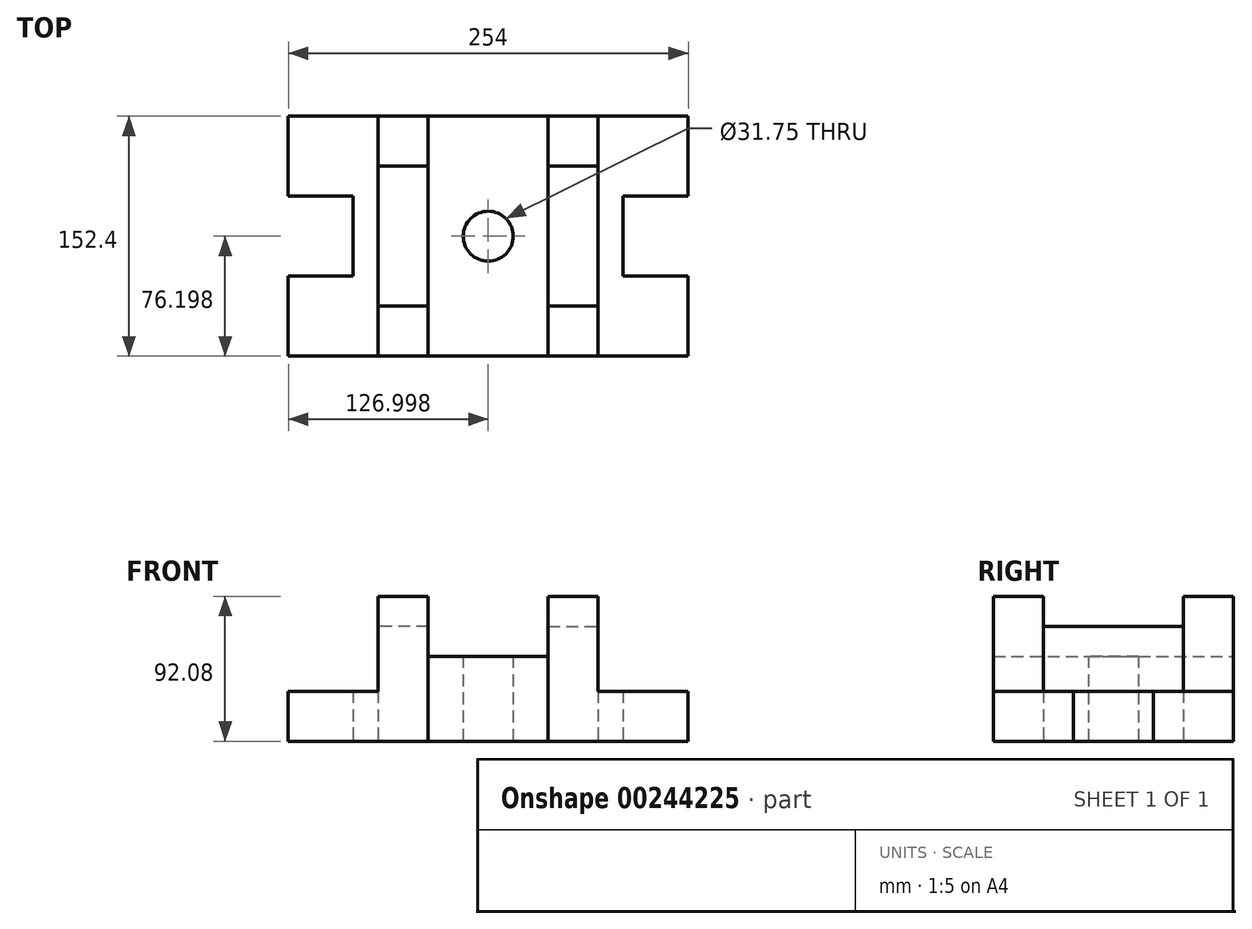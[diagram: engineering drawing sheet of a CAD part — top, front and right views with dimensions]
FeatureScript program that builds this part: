
annotation { "Feature Type Name" : "Feature", "Feature Type Description" : "" }
export const myFeature = defineFeature(function(context is Context, id is Id, definition is map)
    precondition{}
    {
        {
            var Q0;
            Q0=qCreatedBy(makeId("Top.planeOp"),FACE);
            var sketch = newSketch(context, id + "F0", { "sketchPlane" : qUnion([Q0])});
            skLineSegment(sketch, "E0.bottom", {"start": v(-146.62, 99.6) * mm, "end": v(107.38, 99.6) * mm});
            skLineSegment(sketch, "E0.top", {"start": v(-146.62, -52.8) * mm, "end": v(107.38, -52.8) * mm});
            skLineSegment(sketch, "E0.left", {"start": v(-146.62, 99.6) * mm, "end": v(-146.62, -52.8) * mm});
            skLineSegment(sketch, "E0.right", {"start": v(107.38, 99.6) * mm, "end": v(107.38, -52.8) * mm});
            skLineSegment(sketch, "E1", {"start": v(66.1, -2) * mm, "end": v(107.38, -2) * mm});
            skLineSegment(sketch, "E2", {"start": v(66.1, -2) * mm, "end": v(66.1, 48.8) * mm});
            skLineSegment(sketch, "E3", {"start": v(66.1, 48.8) * mm, "end": v(107.38, 48.8) * mm});
            skLineSegment(sketch, "E4", {"start": v(-19.62, -52.8) * mm, "end": v(-19.62, 99.6) * mm, "construction": true});
            skLineSegment(sketch, "E5.MirrorCS", {"start": v(-105.35, -2) * mm, "end": v(-105.35, 48.8) * mm});
            skLineSegment(sketch, "E6.MirrorCS", {"start": v(-105.35, 48.8) * mm, "end": v(-146.62, 48.8) * mm});
            skLineSegment(sketch, "E7.MirrorCS", {"start": v(-105.35, -2) * mm, "end": v(-146.62, -2) * mm});
            skLineSegment(sketch, "E8", {"start": v(50.23, -52.8) * mm, "end": v(50.23, 99.6) * mm});
            skLineSegment(sketch, "E9", {"start": v(18.48, -52.8) * mm, "end": v(18.48, 99.6) * mm});
            skLineSegment(sketch, "E10", {"start": v(18.48, -21.04) * mm, "end": v(50.23, -21.04) * mm});
            skLineSegment(sketch, "E11", {"start": v(18.48, 67.86) * mm, "end": v(50.23, 67.86) * mm});
            skLineSegment(sketch, "E12.MirrorCS", {"start": v(-89.47, -52.8) * mm, "end": v(-89.47, 99.6) * mm});
            skLineSegment(sketch, "E13.MirrorCS", {"start": v(-57.72, -52.8) * mm, "end": v(-57.72, 99.6) * mm});
            skLineSegment(sketch, "E14.MirrorCS", {"start": v(-57.72, 67.86) * mm, "end": v(-89.47, 67.86) * mm});
            skLineSegment(sketch, "E15.MirrorCS", {"start": v(-57.72, -21.04) * mm, "end": v(-89.47, -21.04) * mm});
            skCircle(sketch, "E16", {"center": v(-19.62, 23.4) * mm, "radius": 15.88 * mm});
            skSolve(sketch);
        }
        {
            var Q0;
            {var subQ3=sQuery(id+"F0.wireOp",EDGE,"E1");Q0=makeQuery(id+"F0.imprint","IMPRINT",FACE,{"disambiguationData":[TD([[makeQuery(id+"F0.imprint","IMPRINT",EDGE,{"derivedFrom":subQ3}),-1.0]])]});}
            var Q1;
            Q1=makeQuery(id+"F0.imprint","IMPRINT",FACE,{"disambiguationData":[TD([[makeQuery(id+"F0.imprint","IMPRINT",EDGE,{"derivedFrom":sQuery(id+"F0.wireOp",EDGE,"E5.MirrorCS")}),-1.0]])]});
            extrude(context, id + "F1", {"entities" : qUnion([Q0, Q1]), "depth" : 31.75 * mm});
        }
        {
            var Q0;
            {var subQ5=sQuery(id+"F0.wireOp",EDGE,"E15.MirrorCS");Q0=makeQuery(id+"F0.imprint","IMPRINT",FACE,{"disambiguationData":[TD([[makeQuery(id+"F0.imprint","IMPRINT",EDGE,{"derivedFrom":subQ5}),1.0]])]});}
            var Q1;
            {var subQ5=sQuery(id+"F0.wireOp",EDGE,"E14.MirrorCS");Q1=makeQuery(id+"F0.imprint","IMPRINT",FACE,{"disambiguationData":[TD([[makeQuery(id+"F0.imprint","IMPRINT",EDGE,{"derivedFrom":subQ5}),-1.0]])]});}
            var Q2;
            {var subQ5=sQuery(id+"F0.wireOp",EDGE,"E11");Q2=makeQuery(id+"F0.imprint","IMPRINT",FACE,{"disambiguationData":[TD([[makeQuery(id+"F0.imprint","IMPRINT",EDGE,{"derivedFrom":subQ5}),1.0]])]});}
            var Q3;
            {var subQ5=sQuery(id+"F0.wireOp",EDGE,"E10");Q3=makeQuery(id+"F0.imprint","IMPRINT",FACE,{"disambiguationData":[TD([[makeQuery(id+"F0.imprint","IMPRINT",EDGE,{"derivedFrom":subQ5}),-1.0]])]});}
            extrude(context, id + "F2", {"entities" : qUnion([Q0, Q1, Q2, Q3]), "operationType" : NewBodyOperationType.ADD, "depth" : 92.07 * mm});
        }
        {
            var Q0;
            {var subQ0=sQuery(id+"F0.wireOp",EDGE,"E14.MirrorCS");Q0=makeQuery(id+"F0.imprint","IMPRINT",FACE,{"disambiguationData":[TD([[makeQuery(id+"F0.imprint","IMPRINT",EDGE,{"derivedFrom":subQ0}),1.0]])]});}
            var Q1;
            {var subQ0=sQuery(id+"F0.wireOp",EDGE,"E10");Q1=makeQuery(id+"F0.imprint","IMPRINT",FACE,{"disambiguationData":[TD([[makeQuery(id+"F0.imprint","IMPRINT",EDGE,{"derivedFrom":subQ0}),1.0]])]});}
            extrude(context, id + "F3", {"entities" : qUnion([Q0, Q1]), "depth" : 73.02 * mm});
        }
        {
            var Q0;
            Q0=makeQuery(id+"F0.imprint","IMPRINT",FACE,{"disambiguationData":[TD([[makeQuery(id+"F0.imprint","IMPRINT",EDGE,{"derivedFrom":sQuery(id+"F0.wireOp",EDGE,"E16")}),-1.0]])]});
            extrude(context, id + "F4", {"entities" : qUnion([Q0]), "depth" : 53.97 * mm});
        }
    });
